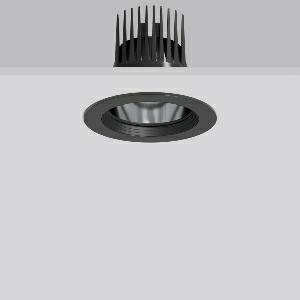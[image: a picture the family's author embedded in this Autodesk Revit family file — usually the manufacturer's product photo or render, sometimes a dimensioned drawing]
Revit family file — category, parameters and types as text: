
# Revit family: heledon_maxi_e_901757_003_1_76_e826
name_source: partatom
category: Lighting Fixtures
units: mm (PartAtom-declared; Revit-internal decimal feet)

## family parameters
Cut with Voids When Loaded = No
Host = Face
Light Source = No
Part Type = Normal
Room Calculation Point = No
Round Connector Dimension = Use Diameter
Shared = No

## types (1)
- HELEDON maxi E (1 x LED Modul 940, 3500 lm, 4000)
    Apparent Load = 25 VA
    Approval mark = CE
    CIE Flux Codes = 100 100 100 100 100
    Color Rendering = 92
    Color Temperature = 4000
    Default Elevation = 1800 mm
    Description = Series: HELEDON maxi
Round recessed downlight. Housing: die-cast aluminium, powder-coated. Black plastic ring and recessed LED to prevent glare from the side. Optical assembly with reflector made of MIRO-Silver with 98% total light reflection for outstanding efficiency - can be changed without tools. Best colour rendering index Ra>90. Suitable for Recessed ceiling mounting. Installation without tools thanks to spring fastening system. Including separate LED converter with connecting cable 600 mm.High quality converter without flickering and stroboscopic effect. Through-wiring box (5 pole) available as accessory. The following accessories can be mounted without use of tools: interchangeable lenses, decorative glasses, honeycomb louvre, clear and frosted diffusers, white interchangeable plastic ring. 
Colour: deep black, matt (RAL 9005)
Diameter: 162 mm
Height: 3 mm
Cut-out diameter: 152 mm
Recess height: 200 mm
Luminaire: recess height: 135 mm
Lamp: LED
Socket: without socket
Colour temperature: 4000K
Colour rendering index (CRI): 92
System power: 25 W
Rated luminous flux: 3500 lm
Luminous efficiency: 140 lm/W
Control gear: Converter, dimmable, DALI
Protection class: II
Type of protection: IP 20
    Height = 0 mm  [stored 0 ft]
    Lamp = 1 x LED Modul 940
    Lamp Light Flux = 3500 lm
    Lamp count = 1
    Length = 162 mm
    Lifetime = 50000 h
    Luminous efficacy = 140 lm/W
    Manufacturer = RZB
    ModVariant = No
    Model = 901757.003.1.76
    Mounting Place = Ceiling
    Mounting Type = Recessed
    Number of Poles = 1
    OnlyDefault = Yes
    Power Factor = 1
    Product Name = HELEDON maxi E
    Product group = Recessed downlights
    ProductGroupID = 402
    Protection Class = Protection class II
    Protection Degree = IP 20
    RLX_Detail_Level = 1
    RLX_Emergency_Light_Flux = 0 lm
    RLX_Emergency_Type = 0
    RLX_Emergency_Type_DB = No
    RlxData = <blob elided: 122445 chars, md5=2ce8ccd1>
    Socket = socket
    Standby Power = 0 W
    System Light Flux = 3500 lm
    System Power = 25 W
    Type Comments = Product without accessories
    Type Image = 901662.003.jpg
    URL = http://relux.com
    VarID = ---
    Voltage = 230 V
    Voltage Range = 220-240 V
    Weight = 0.00 kg
    Width = 0 mm  [stored 0 ft]

note: [stored X ft] marks values corroborated as IEEE doubles in the binary element streams (Revit-internal decimal feet)

## geometry (parser evidence)
native form markers: Blend x4, Sweep x11
no freeform markers — native parametric forms only
